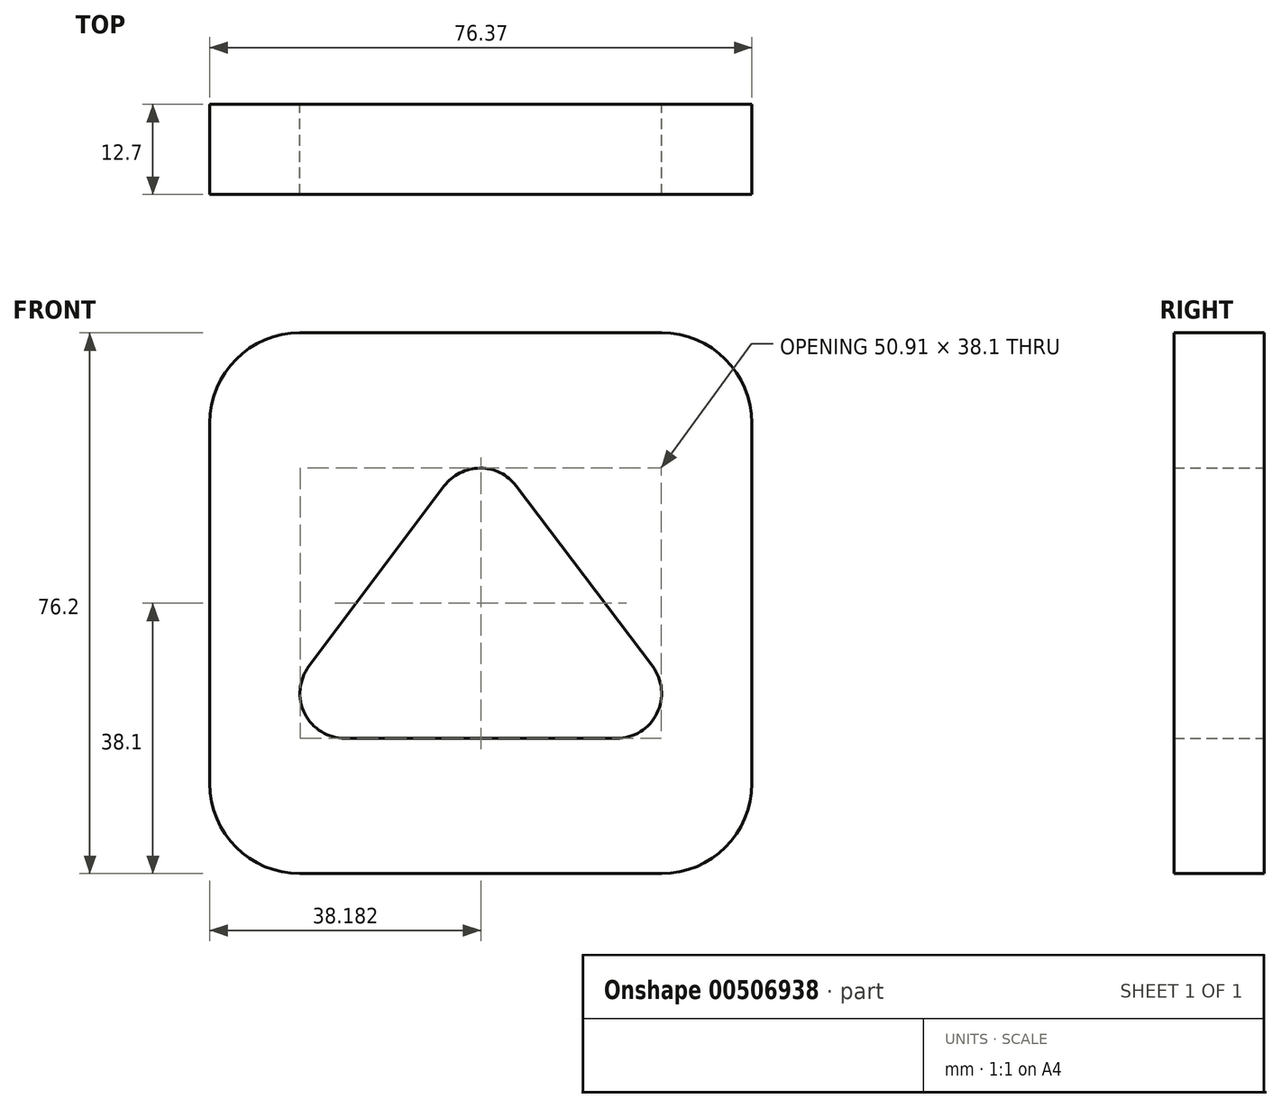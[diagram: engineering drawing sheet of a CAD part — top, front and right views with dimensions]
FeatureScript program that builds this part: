
annotation { "Feature Type Name" : "Feature", "Feature Type Description" : "" }
export const myFeature = defineFeature(function(context is Context, id is Id, definition is map)
    precondition{}
    {
        {
            var Q0;
            Q0=qCreatedBy(makeId("Front.planeOp"),FACE);
            var sketch = newSketch(context, id + "F0", { "sketchPlane" : qUnion([Q0])});
            skLineSegment(sketch, "E0", {"start": v(12.7, 0) * mm, "end": v(63.67, 0) * mm});
            skLineSegment(sketch, "E1", {"start": v(76.37, 12.7) * mm, "end": v(76.37, 63.5) * mm});
            skLineSegment(sketch, "E2", {"start": v(63.67, 76.2) * mm, "end": v(12.7, 76.2) * mm});
            skArc(sketch, "E3", {"start": v(13.97, 29.21) * mm, "mid": v(13.37, 22.56) * mm, "end": v(19.05, 19.05) * mm});
            skArc(sketch, "E4", {"start": v(57.32, 19.05) * mm, "mid": v(63, 22.57) * mm, "end": v(62.38, 29.23) * mm});
            skArc(sketch, "E5", {"start": v(43.16, 54.63) * mm, "mid": v(38.09, 57.15) * mm, "end": v(33.02, 54.61) * mm});
            skLineSegment(sketch, "E6", {"start": v(33.02, 54.61) * mm, "end": v(13.97, 29.2) * mm});
            skLineSegment(sketch, "E7", {"start": v(43.16, 54.63) * mm, "end": v(62.38, 29.23) * mm});
            skLineSegment(sketch, "E8", {"start": v(19.05, 19.05) * mm, "end": v(57.32, 19.05) * mm});
            skArc(sketch, "E9", {"start": v(12.7, 76.2) * mm, "mid": v(3.72, 72.48) * mm, "end": v(0, 63.5) * mm});
            skPoint(sketch, "E10.orphan", {"position": v(0, 76.2) * mm});
            skArc(sketch, "E11", {"start": v(76.37, 63.5) * mm, "mid": v(72.65, 72.48) * mm, "end": v(63.67, 76.2) * mm});
            skLineSegment(sketch, "E12", {"start": v(0, 63.5) * mm, "end": v(0, 12.7) * mm});
            skArc(sketch, "E13", {"start": v(63.67, 0) * mm, "mid": v(72.65, 3.72) * mm, "end": v(76.37, 12.7) * mm});
            skArc(sketch, "E14.trimOffspring", {"start": v(0, 12.7) * mm, "mid": v(3.72, 3.72) * mm, "end": v(12.7, 0) * mm});
            skSolve(sketch);
        }
        {
            var Q0;
            Q0=makeQuery(id+"F0.imprint","IMPRINT",FACE,{"disambiguationData":[TD([[makeQuery(id+"F0.imprint","IMPRINT",EDGE,{"derivedFrom":sQuery(id+"F0.wireOp",EDGE,"E0")}),1.0]])]});
            extrude(context, id + "F1", {"entities" : qUnion([Q0]), "depth" : 12.7 * mm});
        }
    });
